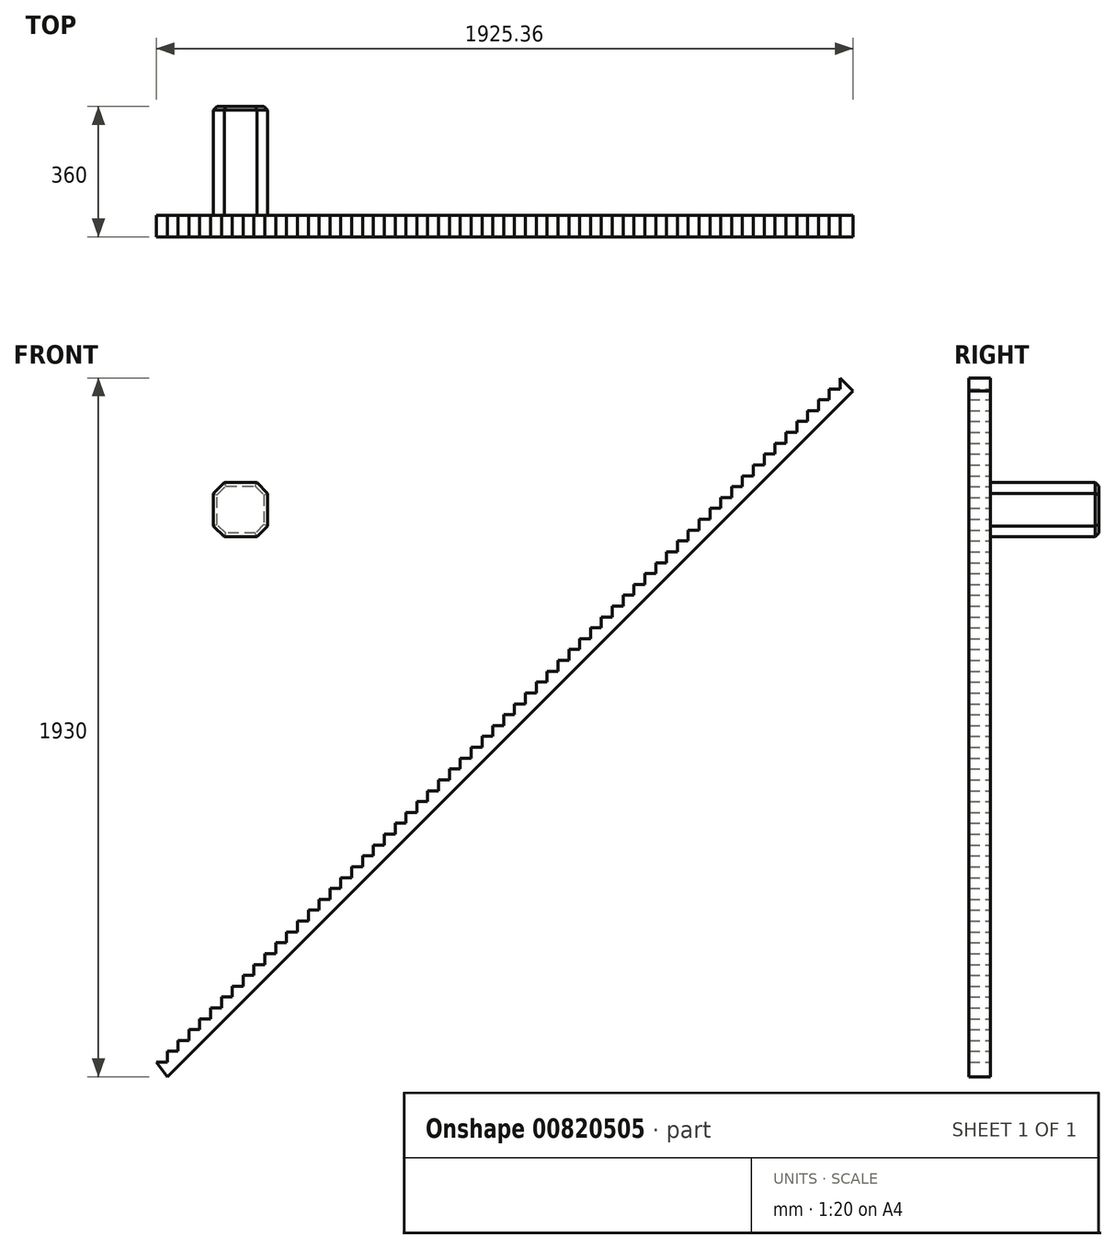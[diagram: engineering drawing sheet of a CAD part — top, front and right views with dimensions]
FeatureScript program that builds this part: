
annotation { "Feature Type Name" : "Feature", "Feature Type Description" : "" }
export const myFeature = defineFeature(function(context is Context, id is Id, definition is map)
    precondition{}
    {
        {
            var Q0;
            Q0=qCreatedBy(makeId("Front.planeOp"),FACE);
            var sketch = newSketch(context, id + "F0", { "sketchPlane" : qUnion([Q0])});
            skLineSegment(sketch, "E0.top", {"start": v(2735, -330.06) * mm, "end": v(2765, -330.06) * mm});
            skLineSegment(sketch, "E0.right", {"start": v(2765, -300.06) * mm, "end": v(2765, -330.06) * mm});
            skLineSegment(sketch, "E1.top", {"start": v(2735, -360.06) * mm, "end": v(2705, -360.06) * mm});
            skLineSegment(sketch, "E1.left", {"start": v(2735, -330.06) * mm, "end": v(2735, -360.06) * mm});
            skLineSegment(sketch, "E2.top", {"start": v(2705, -390.06) * mm, "end": v(2675, -390.06) * mm});
            skLineSegment(sketch, "E2.left", {"start": v(2705, -360.06) * mm, "end": v(2705, -390.06) * mm});
            skLineSegment(sketch, "E3.top", {"start": v(2675, -420.06) * mm, "end": v(2645, -420.06) * mm});
            skLineSegment(sketch, "E3.left", {"start": v(2675, -390.06) * mm, "end": v(2675, -420.06) * mm});
            skLineSegment(sketch, "E4.top", {"start": v(2645, -450.06) * mm, "end": v(2615, -450.06) * mm});
            skLineSegment(sketch, "E4.left", {"start": v(2645, -420.06) * mm, "end": v(2645, -450.06) * mm});
            skLineSegment(sketch, "E5.top", {"start": v(2615, -480.06) * mm, "end": v(2585, -480.06) * mm});
            skLineSegment(sketch, "E5.left", {"start": v(2615, -450.06) * mm, "end": v(2615, -480.06) * mm});
            skLineSegment(sketch, "E6.top", {"start": v(2585, -510.06) * mm, "end": v(2555, -510.06) * mm});
            skLineSegment(sketch, "E6.left", {"start": v(2585, -480.06) * mm, "end": v(2585, -510.06) * mm});
            skLineSegment(sketch, "E7.top", {"start": v(2555, -540.06) * mm, "end": v(2525, -540.06) * mm});
            skLineSegment(sketch, "E7.left", {"start": v(2555, -510.06) * mm, "end": v(2555, -540.06) * mm});
            skLineSegment(sketch, "E8.top", {"start": v(2525, -570.06) * mm, "end": v(2495, -570.06) * mm});
            skLineSegment(sketch, "E8.left", {"start": v(2525, -540.06) * mm, "end": v(2525, -570.06) * mm});
            skLineSegment(sketch, "E9.top", {"start": v(2495, -600.06) * mm, "end": v(2465, -600.06) * mm});
            skLineSegment(sketch, "E9.left", {"start": v(2495, -570.06) * mm, "end": v(2495, -600.06) * mm});
            skLineSegment(sketch, "E10.top", {"start": v(2465, -630.06) * mm, "end": v(2435, -630.06) * mm});
            skLineSegment(sketch, "E10.left", {"start": v(2465, -600.06) * mm, "end": v(2465, -630.06) * mm});
            skLineSegment(sketch, "E11.top", {"start": v(2435, -660.06) * mm, "end": v(2405, -660.06) * mm});
            skLineSegment(sketch, "E11.left", {"start": v(2435, -630.06) * mm, "end": v(2435, -660.06) * mm});
            skLineSegment(sketch, "E12.top", {"start": v(2405, -690.06) * mm, "end": v(2375, -690.06) * mm});
            skLineSegment(sketch, "E12.left", {"start": v(2405, -660.06) * mm, "end": v(2405, -690.06) * mm});
            skLineSegment(sketch, "E13.top", {"start": v(2375, -720.06) * mm, "end": v(2345, -720.06) * mm});
            skLineSegment(sketch, "E13.left", {"start": v(2375, -690.06) * mm, "end": v(2375, -720.06) * mm});
            skLineSegment(sketch, "E14.top", {"start": v(2345, -750.06) * mm, "end": v(2315, -750.06) * mm});
            skLineSegment(sketch, "E14.left", {"start": v(2345, -720.06) * mm, "end": v(2345, -750.06) * mm});
            skLineSegment(sketch, "E15.top", {"start": v(2315, -780.06) * mm, "end": v(2285, -780.06) * mm});
            skLineSegment(sketch, "E15.left", {"start": v(2315, -750.06) * mm, "end": v(2315, -780.06) * mm});
            skLineSegment(sketch, "E16.top", {"start": v(2285, -810.06) * mm, "end": v(2255, -810.06) * mm});
            skLineSegment(sketch, "E16.left", {"start": v(2285, -780.06) * mm, "end": v(2285, -810.06) * mm});
            skLineSegment(sketch, "E17.top", {"start": v(2255, -840.06) * mm, "end": v(2225, -840.06) * mm});
            skLineSegment(sketch, "E17.left", {"start": v(2255, -810.06) * mm, "end": v(2255, -840.06) * mm});
            skLineSegment(sketch, "E18.top", {"start": v(2225, -870.06) * mm, "end": v(2195, -870.06) * mm});
            skLineSegment(sketch, "E18.left", {"start": v(2225, -840.06) * mm, "end": v(2225, -870.06) * mm});
            skLineSegment(sketch, "E19.top", {"start": v(2195, -900.06) * mm, "end": v(2165, -900.06) * mm});
            skLineSegment(sketch, "E19.left", {"start": v(2195, -870.06) * mm, "end": v(2195, -900.06) * mm});
            skLineSegment(sketch, "E20.top", {"start": v(2165, -930.06) * mm, "end": v(2135, -930.06) * mm});
            skLineSegment(sketch, "E20.left", {"start": v(2165, -900.06) * mm, "end": v(2165, -930.06) * mm});
            skLineSegment(sketch, "E21.top", {"start": v(2135, -960.06) * mm, "end": v(2105, -960.06) * mm});
            skLineSegment(sketch, "E21.left", {"start": v(2135, -930.06) * mm, "end": v(2135, -960.06) * mm});
            skLineSegment(sketch, "E22.top", {"start": v(2105, -990.06) * mm, "end": v(2075, -990.06) * mm});
            skLineSegment(sketch, "E22.left", {"start": v(2105, -960.06) * mm, "end": v(2105, -990.06) * mm});
            skLineSegment(sketch, "E23.top", {"start": v(2075, -1020.06) * mm, "end": v(2045, -1020.06) * mm});
            skLineSegment(sketch, "E23.left", {"start": v(2075, -990.06) * mm, "end": v(2075, -1020.06) * mm});
            skLineSegment(sketch, "E24.top", {"start": v(2045, -1050.06) * mm, "end": v(2015, -1050.06) * mm});
            skLineSegment(sketch, "E24.left", {"start": v(2045, -1020.06) * mm, "end": v(2045, -1050.06) * mm});
            skLineSegment(sketch, "E25.top", {"start": v(2015, -1080.06) * mm, "end": v(1985, -1080.06) * mm});
            skLineSegment(sketch, "E25.left", {"start": v(2015, -1050.06) * mm, "end": v(2015, -1080.06) * mm});
            skLineSegment(sketch, "E26.top", {"start": v(1985, -1110.06) * mm, "end": v(1955, -1110.06) * mm});
            skLineSegment(sketch, "E26.left", {"start": v(1985, -1080.06) * mm, "end": v(1985, -1110.06) * mm});
            skLineSegment(sketch, "E27.top", {"start": v(1955, -1140.06) * mm, "end": v(1925, -1140.06) * mm});
            skLineSegment(sketch, "E27.left", {"start": v(1955, -1110.06) * mm, "end": v(1955, -1140.06) * mm});
            skLineSegment(sketch, "E28.top", {"start": v(1925, -1170.06) * mm, "end": v(1895, -1170.06) * mm});
            skLineSegment(sketch, "E28.left", {"start": v(1925, -1140.06) * mm, "end": v(1925, -1170.06) * mm});
            skLineSegment(sketch, "E29.top", {"start": v(1895, -1200.06) * mm, "end": v(1865, -1200.06) * mm});
            skLineSegment(sketch, "E29.left", {"start": v(1895, -1170.06) * mm, "end": v(1895, -1200.06) * mm});
            skLineSegment(sketch, "E30.top", {"start": v(1865, -1230.06) * mm, "end": v(1835, -1230.06) * mm});
            skLineSegment(sketch, "E30.left", {"start": v(1865, -1200.06) * mm, "end": v(1865, -1230.06) * mm});
            skLineSegment(sketch, "E31.top", {"start": v(1835, -1260.06) * mm, "end": v(1805, -1260.06) * mm});
            skLineSegment(sketch, "E31.left", {"start": v(1835, -1230.06) * mm, "end": v(1835, -1260.06) * mm});
            skLineSegment(sketch, "E32.top", {"start": v(1805, -1290.06) * mm, "end": v(1775, -1290.06) * mm});
            skLineSegment(sketch, "E32.left", {"start": v(1805, -1260.06) * mm, "end": v(1805, -1290.06) * mm});
            skLineSegment(sketch, "E33.top", {"start": v(1775, -1320.06) * mm, "end": v(1745, -1320.06) * mm});
            skLineSegment(sketch, "E33.left", {"start": v(1775, -1290.06) * mm, "end": v(1775, -1320.06) * mm});
            skLineSegment(sketch, "E34.top", {"start": v(1745, -1350.06) * mm, "end": v(1715, -1350.06) * mm});
            skLineSegment(sketch, "E34.left", {"start": v(1745, -1320.06) * mm, "end": v(1745, -1350.06) * mm});
            skLineSegment(sketch, "E35.top", {"start": v(1715, -1380.06) * mm, "end": v(1685, -1380.06) * mm});
            skLineSegment(sketch, "E35.left", {"start": v(1715, -1350.06) * mm, "end": v(1715, -1380.06) * mm});
            skLineSegment(sketch, "E36.top", {"start": v(1685, -1410.06) * mm, "end": v(1655, -1410.06) * mm});
            skLineSegment(sketch, "E36.left", {"start": v(1685, -1380.06) * mm, "end": v(1685, -1410.06) * mm});
            skLineSegment(sketch, "E37.top", {"start": v(1655, -1440.06) * mm, "end": v(1625, -1440.06) * mm});
            skLineSegment(sketch, "E37.left", {"start": v(1655, -1410.06) * mm, "end": v(1655, -1440.06) * mm});
            skLineSegment(sketch, "E38.top", {"start": v(1625, -1470.06) * mm, "end": v(1595, -1470.06) * mm});
            skLineSegment(sketch, "E38.left", {"start": v(1625, -1440.06) * mm, "end": v(1625, -1470.06) * mm});
            skLineSegment(sketch, "E39.top", {"start": v(1595, -1500.06) * mm, "end": v(1565, -1500.06) * mm});
            skLineSegment(sketch, "E39.left", {"start": v(1595, -1470.06) * mm, "end": v(1595, -1500.06) * mm});
            skLineSegment(sketch, "E40.top", {"start": v(1565, -1530.06) * mm, "end": v(1535, -1530.06) * mm});
            skLineSegment(sketch, "E40.left", {"start": v(1565, -1500.06) * mm, "end": v(1565, -1530.06) * mm});
            skLineSegment(sketch, "E41.top", {"start": v(1535, -1560.06) * mm, "end": v(1505, -1560.06) * mm});
            skLineSegment(sketch, "E41.left", {"start": v(1535, -1530.06) * mm, "end": v(1535, -1560.06) * mm});
            skLineSegment(sketch, "E42.top", {"start": v(1505, -1590.06) * mm, "end": v(1475, -1590.06) * mm});
            skLineSegment(sketch, "E42.left", {"start": v(1505, -1560.06) * mm, "end": v(1505, -1590.06) * mm});
            skLineSegment(sketch, "E43.top", {"start": v(1475, -1620.06) * mm, "end": v(1445, -1620.06) * mm});
            skLineSegment(sketch, "E43.left", {"start": v(1475, -1590.06) * mm, "end": v(1475, -1620.06) * mm});
            skLineSegment(sketch, "E44.top", {"start": v(1445, -1650.06) * mm, "end": v(1415, -1650.06) * mm});
            skLineSegment(sketch, "E44.left", {"start": v(1445, -1620.06) * mm, "end": v(1445, -1650.06) * mm});
            skLineSegment(sketch, "E45.top", {"start": v(1415, -1680.06) * mm, "end": v(1385, -1680.06) * mm});
            skLineSegment(sketch, "E45.left", {"start": v(1415, -1650.06) * mm, "end": v(1415, -1680.06) * mm});
            skLineSegment(sketch, "E46.top", {"start": v(1385, -1710.06) * mm, "end": v(1355, -1710.06) * mm});
            skLineSegment(sketch, "E46.left", {"start": v(1385, -1680.06) * mm, "end": v(1385, -1710.06) * mm});
            skLineSegment(sketch, "E47.top", {"start": v(1355, -1740.06) * mm, "end": v(1325, -1740.06) * mm});
            skLineSegment(sketch, "E47.left", {"start": v(1355, -1710.06) * mm, "end": v(1355, -1740.06) * mm});
            skLineSegment(sketch, "E48.top", {"start": v(1325, -1770.06) * mm, "end": v(1295, -1770.06) * mm});
            skLineSegment(sketch, "E48.left", {"start": v(1325, -1740.06) * mm, "end": v(1325, -1770.06) * mm});
            skLineSegment(sketch, "E49.top", {"start": v(1295, -1800.06) * mm, "end": v(1265, -1800.06) * mm});
            skLineSegment(sketch, "E49.left", {"start": v(1295, -1770.06) * mm, "end": v(1295, -1800.06) * mm});
            skLineSegment(sketch, "E50.top", {"start": v(1265, -1830.06) * mm, "end": v(1235, -1830.06) * mm});
            skLineSegment(sketch, "E50.left", {"start": v(1265, -1800.06) * mm, "end": v(1265, -1830.06) * mm});
            skLineSegment(sketch, "E51.top", {"start": v(1235, -1860.06) * mm, "end": v(1205, -1860.06) * mm});
            skLineSegment(sketch, "E51.left", {"start": v(1235, -1830.06) * mm, "end": v(1235, -1860.06) * mm});
            skLineSegment(sketch, "E52.top", {"start": v(1205, -1890.06) * mm, "end": v(1175, -1890.06) * mm});
            skLineSegment(sketch, "E52.left", {"start": v(1205, -1860.06) * mm, "end": v(1205, -1890.06) * mm});
            skLineSegment(sketch, "E53.bottom", {"start": v(1175, -1890.06) * mm, "end": v(1175, -1890.06) * mm});
            skLineSegment(sketch, "E54.top", {"start": v(1175, -1920.06) * mm, "end": v(1145, -1920.06) * mm});
            skLineSegment(sketch, "E54.left", {"start": v(1175, -1890.06) * mm, "end": v(1175, -1920.06) * mm});
            skLineSegment(sketch, "E55.top", {"start": v(1145, -1950.06) * mm, "end": v(1115, -1950.06) * mm});
            skLineSegment(sketch, "E55.left", {"start": v(1145, -1920.06) * mm, "end": v(1145, -1950.06) * mm});
            skLineSegment(sketch, "E56.top", {"start": v(1115, -1980.06) * mm, "end": v(1085, -1980.06) * mm});
            skLineSegment(sketch, "E56.left", {"start": v(1115, -1950.06) * mm, "end": v(1115, -1980.06) * mm});
            skLineSegment(sketch, "E57.top", {"start": v(1085, -2010.06) * mm, "end": v(1055, -2010.06) * mm});
            skLineSegment(sketch, "E57.left", {"start": v(1085, -1980.06) * mm, "end": v(1085, -2010.06) * mm});
            skLineSegment(sketch, "E58.top", {"start": v(1055, -2040.06) * mm, "end": v(1025, -2040.06) * mm});
            skLineSegment(sketch, "E58.left", {"start": v(1055, -2010.06) * mm, "end": v(1055, -2040.06) * mm});
            skLineSegment(sketch, "E59.top", {"start": v(1025, -2070.06) * mm, "end": v(995, -2070.06) * mm});
            skLineSegment(sketch, "E59.left", {"start": v(1025, -2040.06) * mm, "end": v(1025, -2070.06) * mm});
            skLineSegment(sketch, "E60.top", {"start": v(995, -2100.06) * mm, "end": v(965, -2100.06) * mm});
            skLineSegment(sketch, "E60.left", {"start": v(995, -2070.06) * mm, "end": v(995, -2100.06) * mm});
            skLineSegment(sketch, "E61.top", {"start": v(965, -2130.06) * mm, "end": v(935, -2130.06) * mm});
            skLineSegment(sketch, "E61.left", {"start": v(965, -2100.06) * mm, "end": v(965, -2130.06) * mm});
            skLineSegment(sketch, "E62.top", {"start": v(935, -2160.06) * mm, "end": v(905, -2160.06) * mm});
            skLineSegment(sketch, "E62.left", {"start": v(935, -2130.06) * mm, "end": v(935, -2160.06) * mm});
            skLineSegment(sketch, "E63.top", {"start": v(905, -2190.06) * mm, "end": v(875, -2190.06) * mm});
            skLineSegment(sketch, "E63.left", {"start": v(905, -2160.06) * mm, "end": v(905, -2190.06) * mm});
            skLineSegment(sketch, "E64", {"start": v(875, -2190.06) * mm, "end": v(905, -2230.06) * mm});
            skLineSegment(sketch, "E65", {"start": v(2765, -300.06) * mm, "end": v(2800.35, -335.41) * mm});
            skLineSegment(sketch, "E66", {"start": v(2800.35, -335.41) * mm, "end": v(905, -2230.06) * mm});
            skSolve(sketch);
        }
        {
            var Q0;
            Q0=makeQuery(id+"F0.imprint","IMPRINT",FACE,{"disambiguationData":[TD([[makeQuery(id+"F0.imprint","IMPRINT",EDGE,{"derivedFrom":sQuery(id+"F0.wireOp",EDGE,"E0.top")}),-1.0]])]});
            extrude(context, id + "F1", {"entities" : qUnion([Q0]), "depth" : 60 * mm, "offsetDistance" : 25 * mm});
        }
        {
            var Q0;
            Q0=makeQuery(id+"F1.opExtrude","CAP_FACE",FACE,{"disambiguationData":[OSD([sQuery(id+"F0.wireOp",EDGE,"E0.top"),sQuery(id+"F0.wireOp",EDGE,"E0.right"),sQuery(id+"F0.wireOp",EDGE,"E1.top"),sQuery(id+"F0.wireOp",EDGE,"E1.left"),sQuery(id+"F0.wireOp",EDGE,"E2.top"),sQuery(id+"F0.wireOp",EDGE,"E2.left"),sQuery(id+"F0.wireOp",EDGE,"E3.top"),sQuery(id+"F0.wireOp",EDGE,"E3.left"),sQuery(id+"F0.wireOp",EDGE,"E4.top"),sQuery(id+"F0.wireOp",EDGE,"E4.left"),sQuery(id+"F0.wireOp",EDGE,"E5.top"),sQuery(id+"F0.wireOp",EDGE,"E5.left"),sQuery(id+"F0.wireOp",EDGE,"E6.top"),sQuery(id+"F0.wireOp",EDGE,"E6.left"),sQuery(id+"F0.wireOp",EDGE,"E7.top"),sQuery(id+"F0.wireOp",EDGE,"E7.left"),sQuery(id+"F0.wireOp",EDGE,"E8.top"),sQuery(id+"F0.wireOp",EDGE,"E8.left"),sQuery(id+"F0.wireOp",EDGE,"E9.top"),sQuery(id+"F0.wireOp",EDGE,"E9.left"),sQuery(id+"F0.wireOp",EDGE,"E10.top"),sQuery(id+"F0.wireOp",EDGE,"E10.left"),sQuery(id+"F0.wireOp",EDGE,"E11.top"),sQuery(id+"F0.wireOp",EDGE,"E11.left"),sQuery(id+"F0.wireOp",EDGE,"E12.top"),sQuery(id+"F0.wireOp",EDGE,"E12.left"),sQuery(id+"F0.wireOp",EDGE,"E13.top"),sQuery(id+"F0.wireOp",EDGE,"E13.left"),sQuery(id+"F0.wireOp",EDGE,"E14.top"),sQuery(id+"F0.wireOp",EDGE,"E14.left"),sQuery(id+"F0.wireOp",EDGE,"E15.top"),sQuery(id+"F0.wireOp",EDGE,"E15.left"),sQuery(id+"F0.wireOp",EDGE,"E16.top"),sQuery(id+"F0.wireOp",EDGE,"E16.left"),sQuery(id+"F0.wireOp",EDGE,"E17.top"),sQuery(id+"F0.wireOp",EDGE,"E17.left"),sQuery(id+"F0.wireOp",EDGE,"E18.top"),sQuery(id+"F0.wireOp",EDGE,"E18.left"),sQuery(id+"F0.wireOp",EDGE,"E19.top"),sQuery(id+"F0.wireOp",EDGE,"E19.left"),sQuery(id+"F0.wireOp",EDGE,"E20.top"),sQuery(id+"F0.wireOp",EDGE,"E20.left"),sQuery(id+"F0.wireOp",EDGE,"E21.top"),sQuery(id+"F0.wireOp",EDGE,"E21.left"),sQuery(id+"F0.wireOp",EDGE,"E22.top"),sQuery(id+"F0.wireOp",EDGE,"E22.left"),sQuery(id+"F0.wireOp",EDGE,"E23.top"),sQuery(id+"F0.wireOp",EDGE,"E23.left"),sQuery(id+"F0.wireOp",EDGE,"E24.top"),sQuery(id+"F0.wireOp",EDGE,"E24.left"),sQuery(id+"F0.wireOp",EDGE,"E25.top"),sQuery(id+"F0.wireOp",EDGE,"E25.left"),sQuery(id+"F0.wireOp",EDGE,"E26.top"),sQuery(id+"F0.wireOp",EDGE,"E26.left"),sQuery(id+"F0.wireOp",EDGE,"E27.top"),sQuery(id+"F0.wireOp",EDGE,"E27.left"),sQuery(id+"F0.wireOp",EDGE,"E28.top"),sQuery(id+"F0.wireOp",EDGE,"E28.left"),sQuery(id+"F0.wireOp",EDGE,"E29.top"),sQuery(id+"F0.wireOp",EDGE,"E29.left"),sQuery(id+"F0.wireOp",EDGE,"E30.top"),sQuery(id+"F0.wireOp",EDGE,"E30.left"),sQuery(id+"F0.wireOp",EDGE,"E31.top"),sQuery(id+"F0.wireOp",EDGE,"E31.left"),sQuery(id+"F0.wireOp",EDGE,"E32.top"),sQuery(id+"F0.wireOp",EDGE,"E32.left"),sQuery(id+"F0.wireOp",EDGE,"E33.top"),sQuery(id+"F0.wireOp",EDGE,"E33.left"),sQuery(id+"F0.wireOp",EDGE,"E34.top"),sQuery(id+"F0.wireOp",EDGE,"E34.left"),sQuery(id+"F0.wireOp",EDGE,"E35.top"),sQuery(id+"F0.wireOp",EDGE,"E35.left"),sQuery(id+"F0.wireOp",EDGE,"E36.top"),sQuery(id+"F0.wireOp",EDGE,"E36.left"),sQuery(id+"F0.wireOp",EDGE,"E37.top"),sQuery(id+"F0.wireOp",EDGE,"E37.left"),sQuery(id+"F0.wireOp",EDGE,"E38.top"),sQuery(id+"F0.wireOp",EDGE,"E38.left"),sQuery(id+"F0.wireOp",EDGE,"E39.top"),sQuery(id+"F0.wireOp",EDGE,"E39.left"),sQuery(id+"F0.wireOp",EDGE,"E40.top"),sQuery(id+"F0.wireOp",EDGE,"E40.left"),sQuery(id+"F0.wireOp",EDGE,"E41.top"),sQuery(id+"F0.wireOp",EDGE,"E41.left"),sQuery(id+"F0.wireOp",EDGE,"E42.top"),sQuery(id+"F0.wireOp",EDGE,"E42.left"),sQuery(id+"F0.wireOp",EDGE,"E43.top"),sQuery(id+"F0.wireOp",EDGE,"E43.left"),sQuery(id+"F0.wireOp",EDGE,"E44.top"),sQuery(id+"F0.wireOp",EDGE,"E44.left"),sQuery(id+"F0.wireOp",EDGE,"E45.top"),sQuery(id+"F0.wireOp",EDGE,"E45.left"),sQuery(id+"F0.wireOp",EDGE,"E46.top"),sQuery(id+"F0.wireOp",EDGE,"E46.left"),sQuery(id+"F0.wireOp",EDGE,"E47.top"),sQuery(id+"F0.wireOp",EDGE,"E47.left"),sQuery(id+"F0.wireOp",EDGE,"E48.top"),sQuery(id+"F0.wireOp",EDGE,"E48.left"),sQuery(id+"F0.wireOp",EDGE,"E49.top"),sQuery(id+"F0.wireOp",EDGE,"E49.left"),sQuery(id+"F0.wireOp",EDGE,"E50.top"),sQuery(id+"F0.wireOp",EDGE,"E50.left"),sQuery(id+"F0.wireOp",EDGE,"E51.top"),sQuery(id+"F0.wireOp",EDGE,"E51.left"),sQuery(id+"F0.wireOp",EDGE,"E52.top"),sQuery(id+"F0.wireOp",EDGE,"E52.left"),sQuery(id+"F0.wireOp",EDGE,"E54.top"),sQuery(id+"F0.wireOp",EDGE,"E54.left"),sQuery(id+"F0.wireOp",EDGE,"E55.top"),sQuery(id+"F0.wireOp",EDGE,"E55.left"),sQuery(id+"F0.wireOp",EDGE,"E56.top"),sQuery(id+"F0.wireOp",EDGE,"E56.left"),sQuery(id+"F0.wireOp",EDGE,"E57.top"),sQuery(id+"F0.wireOp",EDGE,"E57.left"),sQuery(id+"F0.wireOp",EDGE,"E58.top"),sQuery(id+"F0.wireOp",EDGE,"E58.left"),sQuery(id+"F0.wireOp",EDGE,"E59.top"),sQuery(id+"F0.wireOp",EDGE,"E59.left"),sQuery(id+"F0.wireOp",EDGE,"E60.top"),sQuery(id+"F0.wireOp",EDGE,"E60.left"),sQuery(id+"F0.wireOp",EDGE,"E61.top"),sQuery(id+"F0.wireOp",EDGE,"E61.left"),sQuery(id+"F0.wireOp",EDGE,"E62.top"),sQuery(id+"F0.wireOp",EDGE,"E62.left"),sQuery(id+"F0.wireOp",EDGE,"E63.top"),sQuery(id+"F0.wireOp",EDGE,"E63.left"),sQuery(id+"F0.wireOp",EDGE,"E64"),sQuery(id+"F0.wireOp",EDGE,"E65"),sQuery(id+"F0.wireOp",EDGE,"E66")])],"isStart":true});
            var sketch = newSketch(context, id + "F2", { "sketchPlane" : qUnion([Q0])});
            skLineSegment(sketch, "E67.bottom", {"start": v(-1032.82, -738.74) * mm, "end": v(-1182.82, -738.74) * mm});
            skLineSegment(sketch, "E67.top", {"start": v(-1032.82, -588.74) * mm, "end": v(-1182.82, -588.74) * mm});
            skLineSegment(sketch, "E67.left", {"start": v(-1032.82, -738.74) * mm, "end": v(-1032.82, -588.74) * mm});
            skLineSegment(sketch, "E67.right", {"start": v(-1182.82, -738.74) * mm, "end": v(-1182.82, -588.74) * mm});
            skPoint(sketch, "E67.middle", {"position": v(-1107.82, -663.74) * mm});
            skSolve(sketch);
        }
        {
            var Q0;
            Q0=makeQuery(id+"F2.imprint","IMPRINT",FACE,{"disambiguationData":[TD([[makeQuery(id+"F2.imprint","IMPRINT",EDGE,{"derivedFrom":sQuery(id+"F2.wireOp",EDGE,"E67.bottom")}),-1.0]])]});
            extrude(context, id + "F3", {"entities" : qUnion([Q0]), "depth" : 300 * mm, "offsetDistance" : 25 * mm});
        }
        {
            var Q0;
            Q0=makeQuery(id+"F3.opExtrude","SWEPT_EDGE",EDGE,{"disambiguationData":[OSD([sQuery(id+"F2.wireOp",EDGE,"E67.top"),sQuery(id+"F2.wireOp",EDGE,"E67.right")])]});
            var Q1;
            Q1=makeQuery(id+"F3.opExtrude","SWEPT_EDGE",EDGE,{"disambiguationData":[OSD([sQuery(id+"F2.wireOp",EDGE,"E67.top"),sQuery(id+"F2.wireOp",EDGE,"E67.left")])]});
            var Q2;
            Q2=makeQuery(id+"F3.opExtrude","SWEPT_EDGE",EDGE,{"disambiguationData":[OSD([sQuery(id+"F2.wireOp",EDGE,"E67.bottom"),sQuery(id+"F2.wireOp",EDGE,"E67.right")])]});
            var Q3;
            Q3=makeQuery(id+"F3.opExtrude","SWEPT_EDGE",EDGE,{"disambiguationData":[OSD([sQuery(id+"F2.wireOp",EDGE,"E67.bottom"),sQuery(id+"F2.wireOp",EDGE,"E67.left")])]});
            chamfer(context, id + "F4", {"entities" : qUnion([Q0, Q1, Q2, Q3]), "width" : 30 * mm, "tangentPropagation" : true});
        }
        {
            var Q0;
            Q0=makeQuery(id+"F3.opExtrude","CAP_EDGE",EDGE,{"disambiguationData":[OSD([sQuery(id+"F2.wireOp",EDGE,"E67.top")])],"isStart":false});
            var Q1;
            Q1=makeQuery(id+"F3.opExtrude","CAP_EDGE",EDGE,{"disambiguationData":[OSD([sQuery(id+"F2.wireOp",EDGE,"E67.left")])],"isStart":false});
            var Q2;
            Q2=makeQuery(id+"F3.opExtrude","CAP_EDGE",EDGE,{"disambiguationData":[OSD([sQuery(id+"F2.wireOp",EDGE,"E67.bottom")])],"isStart":false});
            var Q3;
            Q3=makeQuery(id+"F3.opExtrude","CAP_EDGE",EDGE,{"disambiguationData":[OSD([sQuery(id+"F2.wireOp",EDGE,"E67.right")])],"isStart":false});
            var Q4;
            {var subQ0=sQuery(id+"F2.wireOp",EDGE,"E67.left");var subQ1=sQuery(id+"F2.wireOp",EDGE,"E67.top");Q4=makeQuery(id+"F4.opChamfer","BLEND_EDGE",EDGE,{"blendedFrom":[makeQuery(id+"F3.opExtrude","SWEPT_EDGE",EDGE,{"disambiguationData":[OSD([subQ1,subQ0])]}),makeQuery(id+"F3.opExtrude","CAP_FACE",FACE,{"disambiguationData":[OSD([sQuery(id+"F2.wireOp",EDGE,"E67.bottom"),subQ1,subQ0,sQuery(id+"F2.wireOp",EDGE,"E67.right")])],"isStart":false})],"blendedInto":[makeQuery(id+"F3.opExtrude","CAP_FACE",FACE,{"disambiguationData":[OSD([sQuery(id+"F2.wireOp",EDGE,"E67.bottom"),subQ1,subQ0,sQuery(id+"F2.wireOp",EDGE,"E67.right")])],"isStart":false})]});}
            var Q5;
            {var subQ0=sQuery(id+"F2.wireOp",EDGE,"E67.right");var subQ1=sQuery(id+"F2.wireOp",EDGE,"E67.top");Q5=makeQuery(id+"F4.opChamfer","BLEND_EDGE",EDGE,{"blendedFrom":[makeQuery(id+"F3.opExtrude","SWEPT_EDGE",EDGE,{"disambiguationData":[OSD([subQ1,subQ0])]}),makeQuery(id+"F3.opExtrude","CAP_FACE",FACE,{"disambiguationData":[OSD([sQuery(id+"F2.wireOp",EDGE,"E67.bottom"),subQ1,sQuery(id+"F2.wireOp",EDGE,"E67.left"),subQ0])],"isStart":false})],"blendedInto":[makeQuery(id+"F3.opExtrude","CAP_FACE",FACE,{"disambiguationData":[OSD([sQuery(id+"F2.wireOp",EDGE,"E67.bottom"),subQ1,sQuery(id+"F2.wireOp",EDGE,"E67.left"),subQ0])],"isStart":false})]});}
            var Q6;
            {var subQ0=sQuery(id+"F2.wireOp",EDGE,"E67.right");var subQ1=sQuery(id+"F2.wireOp",EDGE,"E67.bottom");Q6=makeQuery(id+"F4.opChamfer","BLEND_EDGE",EDGE,{"blendedFrom":[makeQuery(id+"F3.opExtrude","SWEPT_EDGE",EDGE,{"disambiguationData":[OSD([subQ1,subQ0])]}),makeQuery(id+"F3.opExtrude","CAP_FACE",FACE,{"disambiguationData":[OSD([subQ1,sQuery(id+"F2.wireOp",EDGE,"E67.top"),sQuery(id+"F2.wireOp",EDGE,"E67.left"),subQ0])],"isStart":false})],"blendedInto":[makeQuery(id+"F3.opExtrude","CAP_FACE",FACE,{"disambiguationData":[OSD([subQ1,sQuery(id+"F2.wireOp",EDGE,"E67.top"),sQuery(id+"F2.wireOp",EDGE,"E67.left"),subQ0])],"isStart":false})]});}
            var Q7;
            {var subQ0=sQuery(id+"F2.wireOp",EDGE,"E67.left");var subQ1=sQuery(id+"F2.wireOp",EDGE,"E67.bottom");Q7=makeQuery(id+"F4.opChamfer","BLEND_EDGE",EDGE,{"blendedFrom":[makeQuery(id+"F3.opExtrude","SWEPT_EDGE",EDGE,{"disambiguationData":[OSD([subQ1,subQ0])]}),makeQuery(id+"F3.opExtrude","CAP_FACE",FACE,{"disambiguationData":[OSD([subQ1,sQuery(id+"F2.wireOp",EDGE,"E67.top"),subQ0,sQuery(id+"F2.wireOp",EDGE,"E67.right")])],"isStart":false})],"blendedInto":[makeQuery(id+"F3.opExtrude","CAP_FACE",FACE,{"disambiguationData":[OSD([subQ1,sQuery(id+"F2.wireOp",EDGE,"E67.top"),subQ0,sQuery(id+"F2.wireOp",EDGE,"E67.right")])],"isStart":false})]});}
            chamfer(context, id + "F5", {"entities" : qUnion([Q0, Q1, Q2, Q3, Q4, Q5, Q6, Q7]), "width" : 10 * mm, "tangentPropagation" : true});
        }
    });
